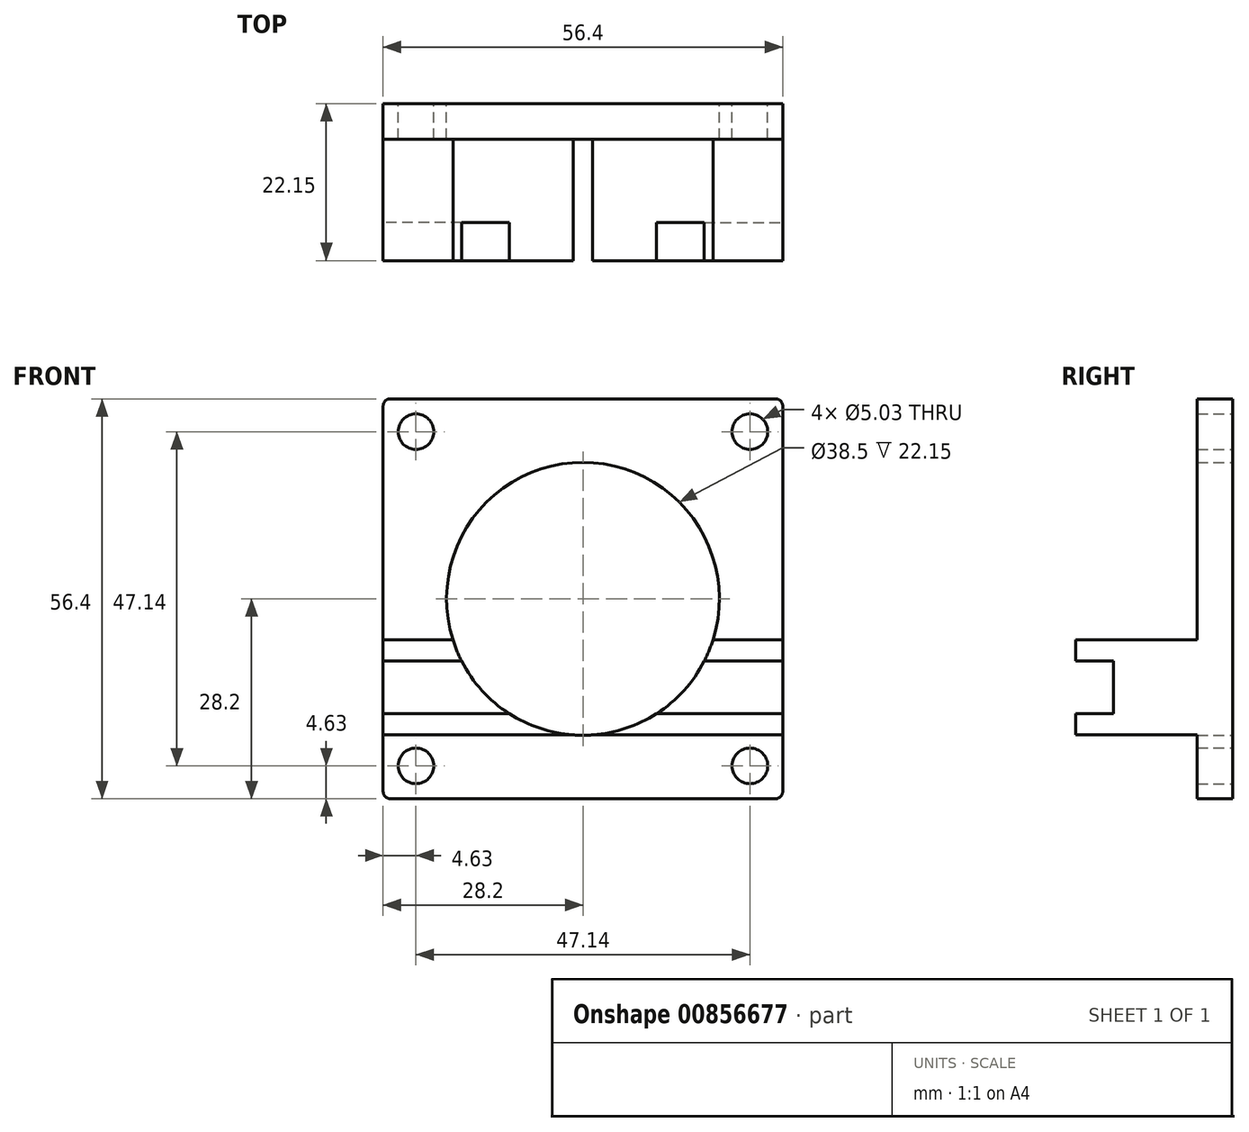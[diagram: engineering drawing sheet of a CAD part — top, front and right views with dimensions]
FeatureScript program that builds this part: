
annotation { "Feature Type Name" : "Feature", "Feature Type Description" : "" }
export const myFeature = defineFeature(function(context is Context, id is Id, definition is map)
    precondition{}
    {
        {
            var Q0;
            Q0=qCreatedBy(makeId("Front.planeOp"),FACE);
            var sketch = newSketch(context, id + "F0", { "sketchPlane" : qUnion([Q0])});
            skLineSegment(sketch, "E0.bottom", {"start": v(27.2, -28.2) * mm, "end": v(-27.2, -28.2) * mm});
            skLineSegment(sketch, "E0.top", {"start": v(27.2, 28.2) * mm, "end": v(-27.2, 28.2) * mm});
            skLineSegment(sketch, "E0.left", {"start": v(28.2, -27.2) * mm, "end": v(28.2, 27.2) * mm});
            skLineSegment(sketch, "E0.right", {"start": v(-28.2, -27.2) * mm, "end": v(-28.2, 27.2) * mm});
            skPoint(sketch, "E0.middle", {"position": v(0, 0) * mm});
            skCircle(sketch, "E1", {"center": v(23.57, -23.57) * mm, "radius": 2.51 * mm});
            skPoint(sketch, "E1.first.point", {"position": v(21.63, -21.97) * mm});
            skPoint(sketch, "E1.second.point", {"position": v(25, -25.64) * mm});
            skPoint(sketch, "E1.third.point", {"position": v(23.84, -21.07) * mm});
            skCircle(sketch, "E2.MirrorC", {"center": v(-23.57, -23.57) * mm, "radius": 2.51 * mm});
            skCircle(sketch, "E3.MirrorC", {"center": v(-23.57, 23.57) * mm, "radius": 2.51 * mm});
            skCircle(sketch, "E4.MirrorC", {"center": v(23.57, 23.57) * mm, "radius": 2.51 * mm});
            skPoint(sketch, "E5.visualSharp", {"position": v(28.2, 28.2) * mm});
            skArc(sketch, "E5.filletArc", {"start": v(28.2, 27.2) * mm, "mid": v(27.9, 27.9) * mm, "end": v(27.2, 28.2) * mm});
            skPoint(sketch, "E6.visualSharp", {"position": v(28.2, -28.2) * mm});
            skArc(sketch, "E6.filletArc", {"start": v(27.2, -28.2) * mm, "mid": v(27.9, -27.9) * mm, "end": v(28.2, -27.2) * mm});
            skPoint(sketch, "E7.visualSharp", {"position": v(-28.2, -28.2) * mm});
            skArc(sketch, "E7.filletArc", {"start": v(-28.2, -27.2) * mm, "mid": v(-27.9, -27.9) * mm, "end": v(-27.2, -28.2) * mm});
            skPoint(sketch, "E8.visualSharp", {"position": v(-28.2, 28.2) * mm});
            skArc(sketch, "E8.filletArc", {"start": v(-27.2, 28.2) * mm, "mid": v(-27.9, 27.9) * mm, "end": v(-28.2, 27.2) * mm});
            skCircle(sketch, "E9", {"center": v(0, 0) * mm, "radius": 19.25 * mm});
            skSolve(sketch);
        }
        {
            var Q0;
            Q0=makeQuery(id+"F0.imprint","IMPRINT",FACE,{"disambiguationData":[TD([[makeQuery(id+"F0.imprint","IMPRINT",EDGE,{"derivedFrom":sQuery(id+"F0.wireOp",EDGE,"E0.bottom")}),-1.0]])]});
            extrude(context, id + "F1", {"entities" : qUnion([Q0]), "depth" : 5 * mm, "offsetDistance" : 25 * mm});
        }
        {
            var Q0;
            Q0=qCreatedBy(makeId("Front.planeOp"),FACE);
            var sketch = newSketch(context, id + "F2", { "sketchPlane" : qUnion([Q0])});
            skLineSegment(sketch, "E10.bottom", {"start": v(0, 0) * mm, "end": v(-65.38, 0) * mm});
            skLineSegment(sketch, "E10.top", {"start": v(0, 46.63) * mm, "end": v(-65.38, 46.63) * mm});
            skLineSegment(sketch, "E10.left", {"start": v(0, 0) * mm, "end": v(0, 46.63) * mm});
            skLineSegment(sketch, "E10.right", {"start": v(-65.38, 0) * mm, "end": v(-65.38, 46.63) * mm});
            skLineSegment(sketch, "E11.bottom", {"start": v(0, 0) * mm, "end": v(-59.84, 0) * mm});
            skLineSegment(sketch, "E11.left", {"start": v(0, 0) * mm, "end": v(0, -51.2) * mm});
            skLineSegment(sketch, "E12.bottom", {"start": v(0, 0) * mm, "end": v(58.85, 0) * mm});
            skLineSegment(sketch, "E12.top", {"start": v(0, 46.63) * mm, "end": v(58.85, 46.63) * mm});
            skLineSegment(sketch, "E12.right", {"start": v(58.85, 0) * mm, "end": v(58.85, 46.63) * mm});
            skSolve(sketch);
        }
        {
            var Q0;
            Q0=makeQuery(id+"F1.opExtrude","SWEPT_FACE",FACE,{"disambiguationData":[OSD([sQuery(id+"F0.wireOp",EDGE,"E0.right")])]});
            var sketch = newSketch(context, id + "F3", { "sketchPlane" : qUnion([Q0])});
            skLineSegment(sketch, "E13.0", {"start": v(5, -27.2) * mm, "end": v(5, 28.2) * mm});
            skLineSegment(sketch, "E14.0", {"start": v(22, -9) * mm, "end": v(17, -9) * mm});
            skLineSegment(sketch, "E15.0", {"start": v(22, -16) * mm, "end": v(17, -16) * mm});
            skLineSegment(sketch, "E16.0", {"start": v(17, -16.05) * mm, "end": v(17, -11.05) * mm});
            skLineSegment(sketch, "E17.0", {"start": v(22, -17) * mm, "end": v(22, -12) * mm});
            skLineSegment(sketch, "E18.bottom", {"start": v(22.15, -8.8) * mm, "end": v(16.8, -8.8) * mm});
            skLineSegment(sketch, "E18.top", {"start": v(22.15, -16.2) * mm, "end": v(16.8, -16.2) * mm});
            skLineSegment(sketch, "E18.right", {"start": v(16.8, -8.8) * mm, "end": v(16.8, -16.2) * mm});
            skLineSegment(sketch, "E19", {"start": v(22.15, -8.8) * mm, "end": v(22.15, -5.8) * mm});
            skLineSegment(sketch, "E20", {"start": v(22.15, -5.8) * mm, "end": v(5, -5.8) * mm});
            skLineSegment(sketch, "E21", {"start": v(5, -5.8) * mm, "end": v(5, -16.2) * mm});
            skLineSegment(sketch, "E22", {"start": v(5, -16.2) * mm, "end": v(5, -19.2) * mm});
            skLineSegment(sketch, "E23", {"start": v(5, -19.2) * mm, "end": v(22.15, -19.2) * mm});
            skLineSegment(sketch, "E24", {"start": v(22.15, -19.2) * mm, "end": v(22.15, -16.2) * mm});
            skPoint(sketch, "E25.0", {"position": v(2.5, -28.2) * mm});
            skLineSegment(sketch, "E26.0", {"start": v(5, -27.2) * mm, "end": v(0, -27.2) * mm});
            skPoint(sketch, "E27.0", {"position": v(0, -27.2) * mm});
            skSolve(sketch);
        }
        {
            var Q0;
            Q0=makeQuery(id+"F3.imprint","IMPRINT",FACE,{"disambiguationData":[TD([[makeQuery(id+"F3.imprint","IMPRINT",EDGE,{"derivedFrom":sQuery(id+"F3.wireOp",EDGE,"E18.bottom")}),-1.0]])]});
            var Q1;
            Q1=makeQuery(id+"F1.opExtrude","SWEPT_FACE",FACE,{"disambiguationData":[OSD([sQuery(id+"F0.wireOp",EDGE,"E9")])]});
            extrude(context, id + "F4", {"entities" : qUnion([Q0]), "endBound" : BoundingType.UP_TO_SURFACE, "oppositeDirection" : true, "depth" : 25 * mm, "endBoundEntityFace" : qUnion([Q1]), "offsetDistance" : 25 * mm});
        }
        {
            var Q0;
            Q0=makeQuery(id+"F4.opExtrude","SWEPT_BODY",BODY,{"disambiguationData":[OSD([sQuery(id+"F3.wireOp",EDGE,"E18.bottom"),sQuery(id+"F3.wireOp",EDGE,"E18.top"),sQuery(id+"F3.wireOp",EDGE,"E18.right"),sQuery(id+"F3.wireOp",EDGE,"E19"),sQuery(id+"F3.wireOp",EDGE,"E20"),sQuery(id+"F3.wireOp",EDGE,"E21"),sQuery(id+"F3.wireOp",EDGE,"E22"),sQuery(id+"F3.wireOp",EDGE,"E23"),sQuery(id+"F3.wireOp",EDGE,"E24")])]});
            var Q1;
            Q1=qCreatedBy(makeId("Right.planeOp"),FACE);
            mirror(context, id + "F5", {"operationType" : NewBodyOperationType.ADD, "entities" : qUnion([Q0]), "mirrorPlane" : qUnion([Q1])});
        }
    });
